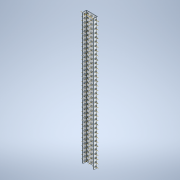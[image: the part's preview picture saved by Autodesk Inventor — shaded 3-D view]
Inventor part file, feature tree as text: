
AUTODESK INVENTOR PART (.ipt)
format: ipt  version: 2020 (Build 240168000, 168)  size: 1,429,504 bytes
history: native  units: in
note: dims shown in document units (in); Inventor stores cm internally (conversion verified against a paired STEP export)
features: other x178, plane x4, pattern_linear x3, sheet_metal_op x1
ambient origin geometry x8: Origin, YZ Plane, XZ Plane, XY Plane, X Axis, Y Axis, Z Axis, Center Point
bodies: Solid1 (feature_tree)
feature tree (186):
  plane  "Work Plane2"
  plane  "Work Plane1"
  other  "Work Point1"
  other  "Work Point2"
  other  "Work Axis1"
  other  "Work Axis2"
  other  "Work Axis3"
  pattern_linear  "Rectangular Pattern1"  Count1=35 Spacing1=0.5in
  pattern_linear  "Rectangular Pattern2"  Count1=35 Spacing1=0.5in
  pattern_linear  "Rectangular Pattern3"  Count1=35 Spacing1=0.5in
  plane  "Work Plane3"
  plane  "Work Plane4"
  other  "Work Point3"
  other  "Work Axis4"
  other  "Work Axis5"
  other  "Work Axis6"
  other  "Work Axis7"
  other  "Work Axis8"
  other  "Work Axis9"
  other  "Work Axis10"
  other  "Work Axis11"
  other  "Work Axis12"
  other  "Work Axis13"
  other  "Work Axis14"
  other  "Work Axis15"
  other  "Work Axis16"
  other  "Work Axis17"
  other  "Work Axis18"
  other  "Work Axis19"
  other  "Work Axis20"
  other  "Work Axis21"
  other  "Work Axis22"
  other  "Work Axis23"
  other  "Work Axis24"
  other  "Work Axis25"
  other  "Work Axis26"
  other  "Work Axis27"
  other  "Work Axis28"
  other  "Work Axis29"
  other  "Work Axis30"
  other  "Work Axis31"
  other  "Work Axis32"
  other  "Work Axis33"
  other  "Work Axis34"
  other  "Work Axis35"
  other  "Work Axis36"
  other  "Work Axis37"
  other  "Work Axis38"
  other  "Work Axis39"
  other  "Work Axis40"
  other  "Work Axis41"
  other  "Work Axis42"
  other  "Work Axis43"
  other  "Work Axis44"
  other  "Work Axis45"
  other  "Work Axis46"
  other  "Work Axis47"
  other  "Work Axis48"
  other  "Work Axis49"
  other  "Work Axis50"
  other  "Work Axis51"
  other  "Work Axis52"
  other  "Work Axis53"
  other  "Work Axis54"
  other  "Work Axis55"
  other  "Work Axis56"
  other  "Work Axis57"
  other  "Work Axis58"
  other  "Work Axis59"
  other  "Work Axis60"
  other  "Work Axis61"
  other  "Work Axis62"
  other  "Work Axis63"
  other  "Work Axis64"
  other  "Work Axis65"
  other  "Work Axis66"
  other  "Work Axis67"
  other  "Work Axis68"
  other  "Work Axis69"
  other  "Work Axis70"
  other  "Work Axis71"
  other  "Work Axis72"
  other  "Work Axis73"
  other  "Work Axis74"
  other  "Work Axis75"
  other  "Work Axis76"
  other  "Work Axis77"
  other  "Work Axis78"
  other  "Work Axis79"
  other  "Work Axis80"
  other  "Work Axis81"
  other  "Work Axis82"
  other  "Work Axis83"
  other  "Work Axis84"
  other  "Work Axis85"
  other  "Work Axis86"
  other  "Work Axis87"
  other  "Work Axis88"
  other  "Work Axis89"
  other  "Work Axis90"
  other  "Work Axis91"
  other  "Work Axis92"
  other  "Work Axis93"
  other  "Work Axis94"
  other  "Work Axis95"
  other  "Work Axis96"
  other  "Work Axis97"
  other  "Work Axis98"
  other  "Work Axis99"
  other  "Work Axis100"
  other  "Work Axis101"
  other  "Work Axis102"
  other  "Work Axis103"
  other  "Work Axis104"
  other  "Work Axis105"
  other  "Work Axis106"
  other  "Work Axis107"
  other  "Work Axis108"
  other  "Work Axis109"
  other  "Work Axis110"
  other  "Work Axis111"
  other  "Work Axis112"
  other  "Work Axis113"
  other  "Work Axis114"
  other  "Work Axis115"
  other  "Work Axis116"
  other  "Work Axis117"
  other  "Work Axis118"
  other  "Work Axis119"
  other  "Work Axis120"
  other  "Work Axis121"
  other  "Work Axis122"
  other  "Work Axis123"
  other  "Work Axis124"
  other  "Work Axis125"
  other  "Work Axis126"
  other  "Work Axis127"
  other  "Work Axis128"
  other  "Work Axis129"
  other  "Work Axis130"
  other  "Work Axis131"
  other  "Work Axis132"
  other  "Work Axis133"
  other  "Work Axis134"
  other  "Work Axis135"
  other  "Work Axis136"
  other  "Work Axis137"
  other  "Work Axis138"
  other  "Work Axis139"
  other  "Work Axis140"
  other  "Work Axis141"
  other  "Work Axis142"
  other  "Work Axis143"
  other  "Work Axis144"
  other  "Work Axis145"
  other  "Work Axis146"
  other  "Work Axis147"
  other  "Work Axis148"
  other  "Work Axis149"
  other  "Work Axis150"
  other  "Work Axis151"
  other  "Work Axis152"
  other  "Work Axis153"
  other  "Work Axis154"
  other  "Work Axis155"
  other  "Work Axis156"
  other  "Work Axis157"
  other  "Work Axis158"
  other  "Work Axis159"
  other  "Work Axis160"
  other  "Work Axis161"
  other  "Work Axis162"
  other  "Work Axis163"
  other  "Work Axis164"
  other  "Work Axis165"
  other  "Work Axis166"
  other  "Work Axis167"
  other  "Work Axis168"
  other  "Work Axis169"
  other  "Work Axis170"
  other  "Work Axis171"
  other  "Work Axis172"
  other  "Work Axis173"
  other  "Work Axis174"
  other  "Work Axis175"
  sheet_metal_op  "Fold1"
